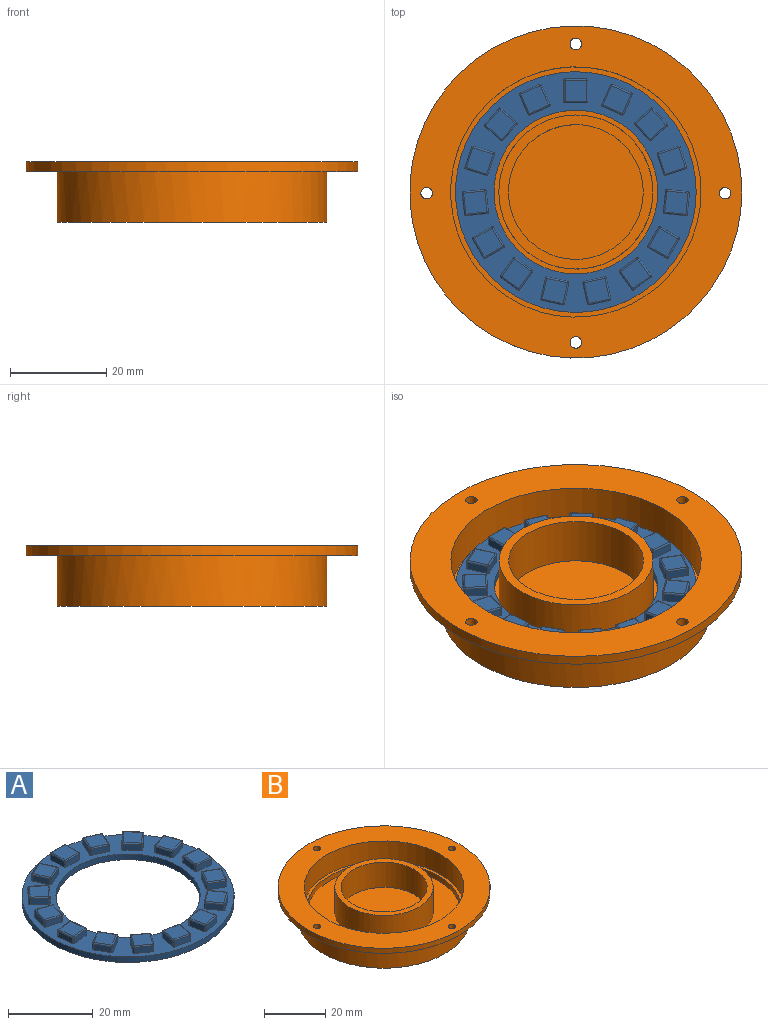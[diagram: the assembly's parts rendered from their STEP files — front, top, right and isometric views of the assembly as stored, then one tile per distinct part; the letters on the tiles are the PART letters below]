
ASSEMBLY  parts=2 mates=1
PART A: 259 faces, bbox 50x50x3.6 mm
  f0: plane 50x50mm, normal (0,0,1), area 681.7mm2, adj f1,f2,f4,f5,f6,f7,f9,f11
  f1: cylinder r=17mm len=34mm, axis (0,0,-1), area 170.9mm2, adj f0,f3
  f2: cylinder r=25mm len=50mm, axis (0,0,-1), area 251.3mm2, adj f0,f3
  f3: plane 50x50mm, normal (0,0,-1), area 1055.6mm2, adj f1,f2
  f4: plane 4.4x1.7mm, normal (0,-1,0), area 7.5mm2, adj f0,f11,f17,f20
  f5: plane 4.4x1.7mm, normal (1,0,0), area 7.5mm2, adj f0,f14,f18,f20
  f6: plane 4.4x1.7mm, normal (0,1,0), area 7.5mm2, adj f0,f9,f13,f14
  f7: plane 4.4x1.7mm, normal (-1,0,0), area 7.5mm2, adj f0,f9,f11,f12
  f8: plane 4.4x4.4mm, normal (0,0,1), area 19.4mm2, adj f12,f13,f17,f18
  f9: cylinder r=0.3mm len=1.7mm, axis (0,0,1), area 0.8mm2, adj f0,f6,f7,f10
  f10: sphere r=0.3mm, area 0.1mm2, adj f9,f12,f13
  f11: cylinder r=0.3mm len=1.7mm, axis (0,0,-1), area 0.8mm2, adj f0,f4,f7,f15
  f12: cylinder r=0.3mm len=4.4mm, axis (0,1,0), area 2.1mm2, adj f7,f8,f10,f15
  f13: cylinder r=0.3mm len=4.4mm, axis (1,0,0), area 2.1mm2, adj f6,f8,f10,f16
  f14: cylinder r=0.3mm len=1.7mm, axis (0,0,-1), area 0.8mm2, adj f0,f5,f6,f16
  f15: sphere r=0.3mm, area 0.1mm2, adj f11,f12,f17
  f16: sphere r=0.3mm, area 0.1mm2, adj f13,f14,f18
  f17: cylinder r=0.3mm len=4.4mm, axis (-1,0,0), area 2.1mm2, adj f4,f8,f15,f19
  f18: cylinder r=0.3mm len=4.4mm, axis (0,-1,0), area 2.1mm2, adj f5,f8,f16,f19
  f19: sphere r=0.3mm, area 0.1mm2, adj f17,f18,f20
  f20: cylinder r=0.3mm len=1.7mm, axis (0,0,1), area 0.8mm2, adj f0,f4,f5,f19
  f21: plane 4.02x1.79mm, normal (0.41,-0.91,0), area 7.5mm2, adj f0,f28,f34,f37
  f22: plane 4.02x1.79mm, normal (0.91,0.41,0), area 7.5mm2, adj f0,f31,f35,f37
  f23: plane 4.02x1.79mm, normal (-0.41,0.91,0), area 7.5mm2, adj f0,f26,f30,f31
  f24: plane 4.02x1.79mm, normal (-0.91,-0.41,0), area 7.5mm2, adj f0,f26,f28,f29
  f25: plane 5.81x5.81mm, normal (0,0,1), area 19.4mm2, adj f29,f30,f34,f35
  f26: cylinder r=0.3mm len=1.7mm, axis (0,0,1), area 0.8mm2, adj f0,f23,f24,f27
  f27: sphere r=0.3mm, area 0.1mm2, adj f26,f29,f30
  f28: cylinder r=0.3mm len=1.7mm, axis (0,0,-1), area 0.8mm2, adj f0,f21,f24,f32
  f29: cylinder r=0.3mm len=4.14mm, axis (-0.41,0.91,0), area 2.1mm2, adj f24,f25,f27,f32
  f30: cylinder r=0.3mm len=4.14mm, axis (0.91,0.41,0), area 2.1mm2, adj f23,f25,f27,f33
  f31: cylinder r=0.3mm len=1.7mm, axis (0,0,-1), area 0.8mm2, adj f0,f22,f23,f33
  f32: sphere r=0.3mm, area 0.1mm2, adj f28,f29,f34
  f33: sphere r=0.3mm, area 0.1mm2, adj f30,f31,f35
  f34: cylinder r=0.3mm len=4.14mm, axis (-0.91,-0.41,0), area 2.1mm2, adj f21,f25,f32,f36
  f35: cylinder r=0.3mm len=4.14mm, axis (0.41,-0.91,0), area 2.1mm2, adj f22,f25,f33,f36
  f36: sphere r=0.3mm, area 0.1mm2, adj f34,f35,f37
  f37: cylinder r=0.3mm len=1.7mm, axis (0,0,1), area 0.8mm2, adj f0,f21,f22,f36
  f38: plane 3.27x2.94mm, normal (0.74,-0.67,0), area 7.5mm2, adj f0,f45,f51,f54
  f39: plane 3.27x2.94mm, normal (0.67,0.74,0), area 7.5mm2, adj f0,f48,f52,f54
  f40: plane 3.27x2.94mm, normal (-0.74,0.67,0), area 7.5mm2, adj f0,f43,f47,f48
  f41: plane 3.27x2.94mm, normal (-0.67,-0.74,0), area 7.5mm2, adj f0,f43,f45,f46
  f42: plane 6.21x6.21mm, normal (0,0,1), area 19.4mm2, adj f46,f47,f51,f52
  f43: cylinder r=0.3mm len=1.7mm, axis (0,0,1), area 0.8mm2, adj f0,f40,f41,f44
  f44: sphere r=0.3mm, area 0.1mm2, adj f43,f46,f47
  f45: cylinder r=0.3mm len=1.7mm, axis (0,0,-1), area 0.8mm2, adj f0,f38,f41,f49
  f46: cylinder r=0.3mm len=3.47mm, axis (-0.74,0.67,0), area 2.1mm2, adj f41,f42,f44,f49
  f47: cylinder r=0.3mm len=3.47mm, axis (0.67,0.74,0), area 2.1mm2, adj f40,f42,f44,f50
  f48: cylinder r=0.3mm len=1.7mm, axis (0,0,-1), area 0.8mm2, adj f0,f39,f40,f50
  f49: sphere r=0.3mm, area 0.1mm2, adj f45,f46,f51
  f50: sphere r=0.3mm, area 0.1mm2, adj f47,f48,f52
  f51: cylinder r=0.3mm len=3.47mm, axis (-0.67,-0.74,0), area 2.1mm2, adj f38,f42,f49,f53
  f52: cylinder r=0.3mm len=3.47mm, axis (0.74,-0.67,0), area 2.1mm2, adj f39,f42,f50,f53
  f53: sphere r=0.3mm, area 0.1mm2, adj f51,f52,f54
  f54: cylinder r=0.3mm len=1.7mm, axis (0,0,1), area 0.8mm2, adj f0,f38,f39,f53
  f55: plane 4.18x1.7mm, normal (0.95,-0.31,0), area 7.5mm2, adj f0,f62,f68,f71
  f56: plane 4.18x1.7mm, normal (0.31,0.95,0), area 7.5mm2, adj f0,f65,f69,f71
  f57: plane 4.18x1.7mm, normal (-0.95,0.31,0), area 7.5mm2, adj f0,f60,f64,f65
  f58: plane 4.18x1.7mm, normal (-0.31,-0.95,0), area 7.5mm2, adj f0,f60,f62,f63
  f59: plane 5.54x5.54mm, normal (0,0,1), area 19.4mm2, adj f63,f64,f68,f69
  f60: cylinder r=0.3mm len=1.7mm, axis (0,0,1), area 0.8mm2, adj f0,f57,f58,f61
  f61: sphere r=0.3mm, area 0.1mm2, adj f60,f63,f64
  f62: cylinder r=0.3mm len=1.7mm, axis (0,0,-1), area 0.8mm2, adj f0,f55,f58,f66
  f63: cylinder r=0.3mm len=4.28mm, axis (-0.95,0.31,0), area 2.1mm2, adj f58,f59,f61,f66
  f64: cylinder r=0.3mm len=4.28mm, axis (0.31,0.95,0), area 2.1mm2, adj f57,f59,f61,f67
  f65: cylinder r=0.3mm len=1.7mm, axis (0,0,-1), area 0.8mm2, adj f0,f56,f57,f67
  f66: sphere r=0.3mm, area 0.1mm2, adj f62,f63,f68
  f67: sphere r=0.3mm, area 0.1mm2, adj f64,f65,f69
  f68: cylinder r=0.3mm len=4.28mm, axis (-0.31,-0.95,0), area 2.1mm2, adj f55,f59,f66,f70
  f69: cylinder r=0.3mm len=4.28mm, axis (0.95,-0.31,0), area 2.1mm2, adj f56,f59,f67,f70
  f70: sphere r=0.3mm, area 0.1mm2, adj f68,f69,f71
  f71: cylinder r=0.3mm len=1.7mm, axis (0,0,1), area 0.8mm2, adj f0,f55,f56,f70
  f72: plane 4.38x1.7mm, normal (0.99,0.1,0), area 7.5mm2, adj f0,f79,f85,f88
  f73: plane 4.38x1.7mm, normal (-0.1,0.99,0), area 7.5mm2, adj f0,f82,f86,f88
  f74: plane 4.38x1.7mm, normal (-0.99,-0.1,0), area 7.5mm2, adj f0,f77,f81,f82
  f75: plane 4.38x1.7mm, normal (0.1,-0.99,0), area 7.5mm2, adj f0,f77,f79,f80
  f76: plane 4.84x4.84mm, normal (0,0,1), area 19.4mm2, adj f80,f81,f85,f86
  f77: cylinder r=0.3mm len=1.7mm, axis (0,0,1), area 0.8mm2, adj f0,f74,f75,f78
  f78: sphere r=0.3mm, area 0.1mm2, adj f77,f80,f81
  f79: cylinder r=0.3mm len=1.7mm, axis (0,0,-1), area 0.8mm2, adj f0,f72,f75,f83
  f80: cylinder r=0.3mm len=4.41mm, axis (-0.99,-0.1,0), area 2.1mm2, adj f75,f76,f78,f83
  f81: cylinder r=0.3mm len=4.41mm, axis (-0.1,0.99,0), area 2.1mm2, adj f74,f76,f78,f84
  f82: cylinder r=0.3mm len=1.7mm, axis (0,0,-1), area 0.8mm2, adj f0,f73,f74,f84
  f83: sphere r=0.3mm, area 0.1mm2, adj f79,f80,f85
  f84: sphere r=0.3mm, area 0.1mm2, adj f81,f82,f86
  f85: cylinder r=0.3mm len=4.41mm, axis (0.1,-0.99,0), area 2.1mm2, adj f72,f76,f83,f87
  f86: cylinder r=0.3mm len=4.41mm, axis (0.99,0.1,0), area 2.1mm2, adj f73,f76,f84,f87
  f87: sphere r=0.3mm, area 0.1mm2, adj f85,f86,f88
  f88: cylinder r=0.3mm len=1.7mm, axis (0,0,1), area 0.8mm2, adj f0,f72,f73,f87
  f89: plane 3.81x2.2mm, normal (0.87,0.5,0), area 7.5mm2, adj f0,f96,f102,f105
  f90: plane 3.81x2.2mm, normal (-0.5,0.87,0), area 7.5mm2, adj f0,f99,f103,f105
  f91: plane 3.81x2.2mm, normal (-0.87,-0.5,0), area 7.5mm2, adj f0,f94,f98,f99
  f92: plane 3.81x2.2mm, normal (0.5,-0.87,0), area 7.5mm2, adj f0,f94,f96,f97
  f93: plane 6.01x6.01mm, normal (0,0,1), area 19.4mm2, adj f97,f98,f102,f103
  f94: cylinder r=0.3mm len=1.7mm, axis (0,0,1), area 0.8mm2, adj f0,f91,f92,f95
  f95: sphere r=0.3mm, area 0.1mm2, adj f94,f97,f98
  f96: cylinder r=0.3mm len=1.7mm, axis (0,0,-1), area 0.8mm2, adj f0,f89,f92,f100
  f97: cylinder r=0.3mm len=3.96mm, axis (-0.87,-0.5,0), area 2.1mm2, adj f92,f93,f95,f100
  f98: cylinder r=0.3mm len=3.96mm, axis (-0.5,0.87,0), area 2.1mm2, adj f91,f93,f95,f101
  f99: cylinder r=0.3mm len=1.7mm, axis (0,0,-1), area 0.8mm2, adj f0,f90,f91,f101
  f100: sphere r=0.3mm, area 0.1mm2, adj f96,f97,f102
  f101: sphere r=0.3mm, area 0.1mm2, adj f98,f99,f103
  f102: cylinder r=0.3mm len=3.96mm, axis (0.5,-0.87,0), area 2.1mm2, adj f89,f93,f100,f104
  f103: cylinder r=0.3mm len=3.96mm, axis (0.87,0.5,0), area 2.1mm2, adj f90,f93,f101,f104
  f104: sphere r=0.3mm, area 0.1mm2, adj f102,f103,f105
  f105: cylinder r=0.3mm len=1.7mm, axis (0,0,1), area 0.8mm2, adj f0,f89,f90,f104
  f106: plane 3.56x2.59mm, normal (0.59,0.81,0), area 7.5mm2, adj f0,f113,f119,f122
  f107: plane 3.56x2.59mm, normal (-0.81,0.59,0), area 7.5mm2, adj f0,f116,f120,f122
  f108: plane 3.56x2.59mm, normal (-0.59,-0.81,0), area 7.5mm2, adj f0,f111,f115,f116
  f109: plane 3.56x2.59mm, normal (0.81,-0.59,0), area 7.5mm2, adj f0,f111,f113,f114
  f110: plane 6.15x6.15mm, normal (0,0,1), area 19.4mm2, adj f114,f115,f119,f120
  f111: cylinder r=0.3mm len=1.7mm, axis (0,0,1), area 0.8mm2, adj f0,f108,f109,f112
  f112: sphere r=0.3mm, area 0.1mm2, adj f111,f114,f115
  f113: cylinder r=0.3mm len=1.7mm, axis (0,0,-1), area 0.8mm2, adj f0,f106,f109,f117
  f114: cylinder r=0.3mm len=3.74mm, axis (-0.59,-0.81,0), area 2.1mm2, adj f109,f110,f112,f117
  f115: cylinder r=0.3mm len=3.74mm, axis (-0.81,0.59,0), area 2.1mm2, adj f108,f110,f112,f118
  f116: cylinder r=0.3mm len=1.7mm, axis (0,0,-1), area 0.8mm2, adj f0,f107,f108,f118
  f117: sphere r=0.3mm, area 0.1mm2, adj f113,f114,f119
  f118: sphere r=0.3mm, area 0.1mm2, adj f115,f116,f120
  f119: cylinder r=0.3mm len=3.74mm, axis (0.81,-0.59,0), area 2.1mm2, adj f106,f110,f117,f121
  f120: cylinder r=0.3mm len=3.74mm, axis (0.59,0.81,0), area 2.1mm2, adj f107,f110,f118,f121
  f121: sphere r=0.3mm, area 0.1mm2, adj f119,f120,f122
  f122: cylinder r=0.3mm len=1.7mm, axis (0,0,1), area 0.8mm2, adj f0,f106,f107,f121
  f123: plane 4.3x1.7mm, normal (0.21,0.98,0), area 7.5mm2, adj f0,f130,f136,f139
  f124: plane 4.3x1.7mm, normal (-0.98,0.21,0), area 7.5mm2, adj f0,f133,f137,f139
  f125: plane 4.3x1.7mm, normal (-0.21,-0.98,0), area 7.5mm2, adj f0,f128,f132,f133
  f126: plane 4.3x1.7mm, normal (0.98,-0.21,0), area 7.5mm2, adj f0,f128,f130,f131
  f127: plane 5.22x5.22mm, normal (0,0,1), area 19.4mm2, adj f131,f132,f136,f137
  f128: cylinder r=0.3mm len=1.7mm, axis (0,0,1), area 0.8mm2, adj f0,f125,f126,f129
  f129: sphere r=0.3mm, area 0.1mm2, adj f128,f131,f132
  f130: cylinder r=0.3mm len=1.7mm, axis (0,0,-1), area 0.8mm2, adj f0,f123,f126,f134
  f131: cylinder r=0.3mm len=4.37mm, axis (-0.21,-0.98,0), area 2.1mm2, adj f126,f127,f129,f134
  f132: cylinder r=0.3mm len=4.37mm, axis (-0.98,0.21,0), area 2.1mm2, adj f125,f127,f129,f135
  f133: cylinder r=0.3mm len=1.7mm, axis (0,0,-1), area 0.8mm2, adj f0,f124,f125,f135
  f134: sphere r=0.3mm, area 0.1mm2, adj f130,f131,f136
  f135: sphere r=0.3mm, area 0.1mm2, adj f132,f133,f137
  f136: cylinder r=0.3mm len=4.37mm, axis (0.98,-0.21,0), area 2.1mm2, adj f123,f127,f134,f138
  f137: cylinder r=0.3mm len=4.37mm, axis (0.21,0.98,0), area 2.1mm2, adj f124,f127,f135,f138
  f138: sphere r=0.3mm, area 0.1mm2, adj f136,f137,f139
  f139: cylinder r=0.3mm len=1.7mm, axis (0,0,1), area 0.8mm2, adj f0,f123,f124,f138
  f140: plane 4.3x1.7mm, normal (-0.21,0.98,0), area 7.5mm2, adj f0,f147,f153,f156
  f141: plane 4.3x1.7mm, normal (-0.98,-0.21,0), area 7.5mm2, adj f0,f150,f154,f156
  f142: plane 4.3x1.7mm, normal (0.21,-0.98,0), area 7.5mm2, adj f0,f145,f149,f150
  f143: plane 4.3x1.7mm, normal (0.98,0.21,0), area 7.5mm2, adj f0,f145,f147,f148
  f144: plane 5.22x5.22mm, normal (0,0,1), area 19.4mm2, adj f148,f149,f153,f154
  f145: cylinder r=0.3mm len=1.7mm, axis (0,0,1), area 0.8mm2, adj f0,f142,f143,f146
  f146: sphere r=0.3mm, area 0.1mm2, adj f145,f148,f149
  f147: cylinder r=0.3mm len=1.7mm, axis (0,0,-1), area 0.8mm2, adj f0,f140,f143,f151
  f148: cylinder r=0.3mm len=4.37mm, axis (0.21,-0.98,0), area 2.1mm2, adj f143,f144,f146,f151
  f149: cylinder r=0.3mm len=4.37mm, axis (-0.98,-0.21,0), area 2.1mm2, adj f142,f144,f146,f152
  f150: cylinder r=0.3mm len=1.7mm, axis (0,0,-1), area 0.8mm2, adj f0,f141,f142,f152
  f151: sphere r=0.3mm, area 0.1mm2, adj f147,f148,f153
  f152: sphere r=0.3mm, area 0.1mm2, adj f149,f150,f154
  f153: cylinder r=0.3mm len=4.37mm, axis (0.98,0.21,0), area 2.1mm2, adj f140,f144,f151,f155
  f154: cylinder r=0.3mm len=4.37mm, axis (-0.21,0.98,0), area 2.1mm2, adj f141,f144,f152,f155
  f155: sphere r=0.3mm, area 0.1mm2, adj f153,f154,f156
  f156: cylinder r=0.3mm len=1.7mm, axis (0,0,1), area 0.8mm2, adj f0,f140,f141,f155
  f157: plane 3.56x2.59mm, normal (-0.59,0.81,0), area 7.5mm2, adj f0,f164,f170,f173
  f158: plane 3.56x2.59mm, normal (-0.81,-0.59,0), area 7.5mm2, adj f0,f167,f171,f173
  f159: plane 3.56x2.59mm, normal (0.59,-0.81,0), area 7.5mm2, adj f0,f162,f166,f167
  f160: plane 3.56x2.59mm, normal (0.81,0.59,0), area 7.5mm2, adj f0,f162,f164,f165
  f161: plane 6.15x6.15mm, normal (0,0,1), area 19.4mm2, adj f165,f166,f170,f171
  f162: cylinder r=0.3mm len=1.7mm, axis (0,0,1), area 0.8mm2, adj f0,f159,f160,f163
  f163: sphere r=0.3mm, area 0.1mm2, adj f162,f165,f166
  f164: cylinder r=0.3mm len=1.7mm, axis (0,0,-1), area 0.8mm2, adj f0,f157,f160,f168
  f165: cylinder r=0.3mm len=3.74mm, axis (0.59,-0.81,0), area 2.1mm2, adj f160,f161,f163,f168
  f166: cylinder r=0.3mm len=3.74mm, axis (-0.81,-0.59,0), area 2.1mm2, adj f159,f161,f163,f169
  f167: cylinder r=0.3mm len=1.7mm, axis (0,0,-1), area 0.8mm2, adj f0,f158,f159,f169
  f168: sphere r=0.3mm, area 0.1mm2, adj f164,f165,f170
  f169: sphere r=0.3mm, area 0.1mm2, adj f166,f167,f171
  f170: cylinder r=0.3mm len=3.74mm, axis (0.81,0.59,0), area 2.1mm2, adj f157,f161,f168,f172
  f171: cylinder r=0.3mm len=3.74mm, axis (-0.59,0.81,0), area 2.1mm2, adj f158,f161,f169,f172
  f172: sphere r=0.3mm, area 0.1mm2, adj f170,f171,f173
  f173: cylinder r=0.3mm len=1.7mm, axis (0,0,1), area 0.8mm2, adj f0,f157,f158,f172
  f174: plane 3.81x2.2mm, normal (-0.87,0.5,0), area 7.5mm2, adj f0,f181,f187,f190
  f175: plane 3.81x2.2mm, normal (-0.5,-0.87,0), area 7.5mm2, adj f0,f184,f188,f190
  f176: plane 3.81x2.2mm, normal (0.87,-0.5,0), area 7.5mm2, adj f0,f179,f183,f184
  f177: plane 3.81x2.2mm, normal (0.5,0.87,0), area 7.5mm2, adj f0,f179,f181,f182
  f178: plane 6.01x6.01mm, normal (0,0,1), area 19.4mm2, adj f182,f183,f187,f188
  f179: cylinder r=0.3mm len=1.7mm, axis (0,0,1), area 0.8mm2, adj f0,f176,f177,f180
  f180: sphere r=0.3mm, area 0.1mm2, adj f179,f182,f183
  f181: cylinder r=0.3mm len=1.7mm, axis (0,0,-1), area 0.8mm2, adj f0,f174,f177,f185
  f182: cylinder r=0.3mm len=3.96mm, axis (0.87,-0.5,0), area 2.1mm2, adj f177,f178,f180,f185
  f183: cylinder r=0.3mm len=3.96mm, axis (-0.5,-0.87,0), area 2.1mm2, adj f176,f178,f180,f186
  f184: cylinder r=0.3mm len=1.7mm, axis (0,0,-1), area 0.8mm2, adj f0,f175,f176,f186
  f185: sphere r=0.3mm, area 0.1mm2, adj f181,f182,f187
  f186: sphere r=0.3mm, area 0.1mm2, adj f183,f184,f188
  f187: cylinder r=0.3mm len=3.96mm, axis (0.5,0.87,0), area 2.1mm2, adj f174,f178,f185,f189
  f188: cylinder r=0.3mm len=3.96mm, axis (-0.87,0.5,0), area 2.1mm2, adj f175,f178,f186,f189
  f189: sphere r=0.3mm, area 0.1mm2, adj f187,f188,f190
  f190: cylinder r=0.3mm len=1.7mm, axis (0,0,1), area 0.8mm2, adj f0,f174,f175,f189
  f191: plane 4.38x1.7mm, normal (-0.99,0.1,0), area 7.5mm2, adj f0,f198,f204,f207
  f192: plane 4.38x1.7mm, normal (-0.1,-0.99,0), area 7.5mm2, adj f0,f201,f205,f207
  f193: plane 4.38x1.7mm, normal (0.99,-0.1,0), area 7.5mm2, adj f0,f196,f200,f201
  f194: plane 4.38x1.7mm, normal (0.1,0.99,0), area 7.5mm2, adj f0,f196,f198,f199
  f195: plane 4.84x4.84mm, normal (0,0,1), area 19.4mm2, adj f199,f200,f204,f205
  f196: cylinder r=0.3mm len=1.7mm, axis (0,0,1), area 0.8mm2, adj f0,f193,f194,f197
  f197: sphere r=0.3mm, area 0.1mm2, adj f196,f199,f200
  f198: cylinder r=0.3mm len=1.7mm, axis (0,0,-1), area 0.8mm2, adj f0,f191,f194,f202
  f199: cylinder r=0.3mm len=4.41mm, axis (0.99,-0.1,0), area 2.1mm2, adj f194,f195,f197,f202
  f200: cylinder r=0.3mm len=4.41mm, axis (-0.1,-0.99,0), area 2.1mm2, adj f193,f195,f197,f203
  f201: cylinder r=0.3mm len=1.7mm, axis (0,0,-1), area 0.8mm2, adj f0,f192,f193,f203
  f202: sphere r=0.3mm, area 0.1mm2, adj f198,f199,f204
  f203: sphere r=0.3mm, area 0.1mm2, adj f200,f201,f205
  f204: cylinder r=0.3mm len=4.41mm, axis (0.1,0.99,0), area 2.1mm2, adj f191,f195,f202,f206
  f205: cylinder r=0.3mm len=4.41mm, axis (-0.99,0.1,0), area 2.1mm2, adj f192,f195,f203,f206
  f206: sphere r=0.3mm, area 0.1mm2, adj f204,f205,f207
  f207: cylinder r=0.3mm len=1.7mm, axis (0,0,1), area 0.8mm2, adj f0,f191,f192,f206
  f208: plane 4.18x1.7mm, normal (-0.95,-0.31,0), area 7.5mm2, adj f0,f215,f221,f224
  f209: plane 4.18x1.7mm, normal (0.31,-0.95,0), area 7.5mm2, adj f0,f218,f222,f224
  f210: plane 4.18x1.7mm, normal (0.95,0.31,0), area 7.5mm2, adj f0,f213,f217,f218
  f211: plane 4.18x1.7mm, normal (-0.31,0.95,0), area 7.5mm2, adj f0,f213,f215,f216
  f212: plane 5.54x5.54mm, normal (0,0,1), area 19.4mm2, adj f216,f217,f221,f222
  f213: cylinder r=0.3mm len=1.7mm, axis (0,0,1), area 0.8mm2, adj f0,f210,f211,f214
  f214: sphere r=0.3mm, area 0.1mm2, adj f213,f216,f217
  f215: cylinder r=0.3mm len=1.7mm, axis (0,0,-1), area 0.8mm2, adj f0,f208,f211,f219
  f216: cylinder r=0.3mm len=4.28mm, axis (0.95,0.31,0), area 2.1mm2, adj f211,f212,f214,f219
  f217: cylinder r=0.3mm len=4.28mm, axis (0.31,-0.95,0), area 2.1mm2, adj f210,f212,f214,f220
  f218: cylinder r=0.3mm len=1.7mm, axis (0,0,-1), area 0.8mm2, adj f0,f209,f210,f220
  f219: sphere r=0.3mm, area 0.1mm2, adj f215,f216,f221
  f220: sphere r=0.3mm, area 0.1mm2, adj f217,f218,f222
  f221: cylinder r=0.3mm len=4.28mm, axis (-0.31,0.95,0), area 2.1mm2, adj f208,f212,f219,f223
  f222: cylinder r=0.3mm len=4.28mm, axis (-0.95,-0.31,0), area 2.1mm2, adj f209,f212,f220,f223
  f223: sphere r=0.3mm, area 0.1mm2, adj f221,f222,f224
  f224: cylinder r=0.3mm len=1.7mm, axis (0,0,1), area 0.8mm2, adj f0,f208,f209,f223
  f225: plane 3.27x2.94mm, normal (-0.74,-0.67,0), area 7.5mm2, adj f0,f232,f238,f241
  f226: plane 3.27x2.94mm, normal (0.67,-0.74,0), area 7.5mm2, adj f0,f235,f239,f241
  f227: plane 3.27x2.94mm, normal (0.74,0.67,0), area 7.5mm2, adj f0,f230,f234,f235
  f228: plane 3.27x2.94mm, normal (-0.67,0.74,0), area 7.5mm2, adj f0,f230,f232,f233
  f229: plane 6.21x6.21mm, normal (0,0,1), area 19.4mm2, adj f233,f234,f238,f239
  f230: cylinder r=0.3mm len=1.7mm, axis (0,0,1), area 0.8mm2, adj f0,f227,f228,f231
  f231: sphere r=0.3mm, area 0.1mm2, adj f230,f233,f234
  f232: cylinder r=0.3mm len=1.7mm, axis (0,0,-1), area 0.8mm2, adj f0,f225,f228,f236
  f233: cylinder r=0.3mm len=3.47mm, axis (0.74,0.67,0), area 2.1mm2, adj f228,f229,f231,f236
  f234: cylinder r=0.3mm len=3.47mm, axis (0.67,-0.74,0), area 2.1mm2, adj f227,f229,f231,f237
  f235: cylinder r=0.3mm len=1.7mm, axis (0,0,-1), area 0.8mm2, adj f0,f226,f227,f237
  f236: sphere r=0.3mm, area 0.1mm2, adj f232,f233,f238
  f237: sphere r=0.3mm, area 0.1mm2, adj f234,f235,f239
  f238: cylinder r=0.3mm len=3.47mm, axis (-0.67,0.74,0), area 2.1mm2, adj f225,f229,f236,f240
  f239: cylinder r=0.3mm len=3.47mm, axis (-0.74,-0.67,0), area 2.1mm2, adj f226,f229,f237,f240
  f240: sphere r=0.3mm, area 0.1mm2, adj f238,f239,f241
  f241: cylinder r=0.3mm len=1.7mm, axis (0,0,1), area 0.8mm2, adj f0,f225,f226,f240
  f242: plane 4.02x1.79mm, normal (-0.41,-0.91,0), area 7.5mm2, adj f0,f249,f255,f258
  f243: plane 4.02x1.79mm, normal (0.91,-0.41,0), area 7.5mm2, adj f0,f252,f256,f258
  f244: plane 4.02x1.79mm, normal (0.41,0.91,0), area 7.5mm2, adj f0,f247,f251,f252
  f245: plane 4.02x1.79mm, normal (-0.91,0.41,0), area 7.5mm2, adj f0,f247,f249,f250
  f246: plane 5.81x5.81mm, normal (0,0,1), area 19.4mm2, adj f250,f251,f255,f256
  f247: cylinder r=0.3mm len=1.7mm, axis (0,0,1), area 0.8mm2, adj f0,f244,f245,f248
  f248: sphere r=0.3mm, area 0.1mm2, adj f247,f250,f251
  f249: cylinder r=0.3mm len=1.7mm, axis (0,0,-1), area 0.8mm2, adj f0,f242,f245,f253
  f250: cylinder r=0.3mm len=4.14mm, axis (0.41,0.91,0), area 2.1mm2, adj f245,f246,f248,f253
  f251: cylinder r=0.3mm len=4.14mm, axis (0.91,-0.41,0), area 2.1mm2, adj f244,f246,f248,f254
  f252: cylinder r=0.3mm len=1.7mm, axis (0,0,-1), area 0.8mm2, adj f0,f243,f244,f254
  f253: sphere r=0.3mm, area 0.1mm2, adj f249,f250,f255
  f254: sphere r=0.3mm, area 0.1mm2, adj f251,f252,f256
  f255: cylinder r=0.3mm len=4.14mm, axis (-0.91,0.41,0), area 2.1mm2, adj f242,f246,f253,f257
  f256: cylinder r=0.3mm len=4.14mm, axis (-0.41,-0.91,0), area 2.1mm2, adj f243,f246,f254,f257
  f257: sphere r=0.3mm, area 0.1mm2, adj f255,f256,f258
  f258: cylinder r=0.3mm len=1.7mm, axis (0,0,1), area 0.8mm2, adj f0,f242,f243,f257
PART B: 18 faces, bbox 69x69x12.5 mm
  f0: cylinder r=28mm len=56mm, axis (0,0,1), area 1847.3mm2, adj f6,f13
  f1: plane 52x52mm, normal (0,0,1), area 160.2mm2, adj f2,f4
  f2: cylinder r=25mm len=50mm, axis (0,0,1), area 314.2mm2, adj f1,f3
  f3: plane 50x50mm, normal (0,0,1), area 1156.1mm2, adj f2,f7,f16
  f4: cylinder r=26mm len=52mm, axis (0,0,-1), area 1306.9mm2, adj f1,f5
  f5: plane 69x69mm, normal (0,0,1), area 1597.5mm2, adj f4,f8,f9,f10,f11,f12
  f6: plane 56x56mm, normal (0,0,-1), area 2459.9mm2, adj f0,f7
  f7: cylinder r=1mm len=2.5mm, axis (0,0,-1), area 15.7mm2, adj f3,f6
  f8: cylinder r=1.2mm len=2.4mm, axis (0,0,1), area 15.1mm2, adj f5,f13
  f9: cylinder r=1.2mm len=2.4mm, axis (0,0,1), area 15.1mm2, adj f5,f13
  f10: cylinder r=1.2mm len=2.4mm, axis (0,0,1), area 15.1mm2, adj f5,f13
  f11: cylinder r=1.2mm len=2.4mm, axis (0,0,1), area 15.1mm2, adj f5,f13
  f12: cylinder r=34.5mm len=69mm, axis (0,0,1), area 433.5mm2, adj f5,f13
  f13: plane 69x69mm, normal (0,0,-1), area 1258.2mm2, adj f0,f8,f9,f10,f11,f12
  f14: plane 32x32mm, normal (0,0,1), area 188.5mm2, adj f15,f16
  f15: cylinder r=14mm len=28mm, axis (0,0,-1), area 879.6mm2, adj f14,f17
  f16: cylinder r=16mm len=32mm, axis (0,0,-1), area 1005.3mm2, adj f3,f14
  f17: plane 28x28mm, normal (0,0,1), area 615.8mm2, adj f15
PLACE A at identity fixed
PLACE B at identity
MATE fastened A.f1 <-> B.f0  axis (0,0,-1) through (0,0,0)mm
